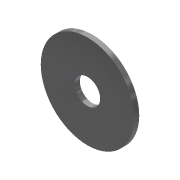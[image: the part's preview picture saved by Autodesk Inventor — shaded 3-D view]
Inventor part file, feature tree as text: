
AUTODESK INVENTOR PART (.ipt)
format: ipt  version: 2013 (Build 170138000, 138)  size: 74,752 bytes
history: native  units: in
note: dims shown in document units (in); Inventor stores cm internally (conversion verified against a paired STEP export)
features: extrude x1, sketch x1
ambient origin geometry x8: Origin, YZ Plane, XZ Plane, XY Plane, X Axis, Y Axis, Z Axis, Center Point
bodies: Solid1 (feature_tree)
feature tree (2):
  extrude  "Extrusion1"  Depth=0.2031in
  sketch  "Sketch1"  dims[d0=0.75in d1=0.2031in d2=0.04in d3=0.0in]
